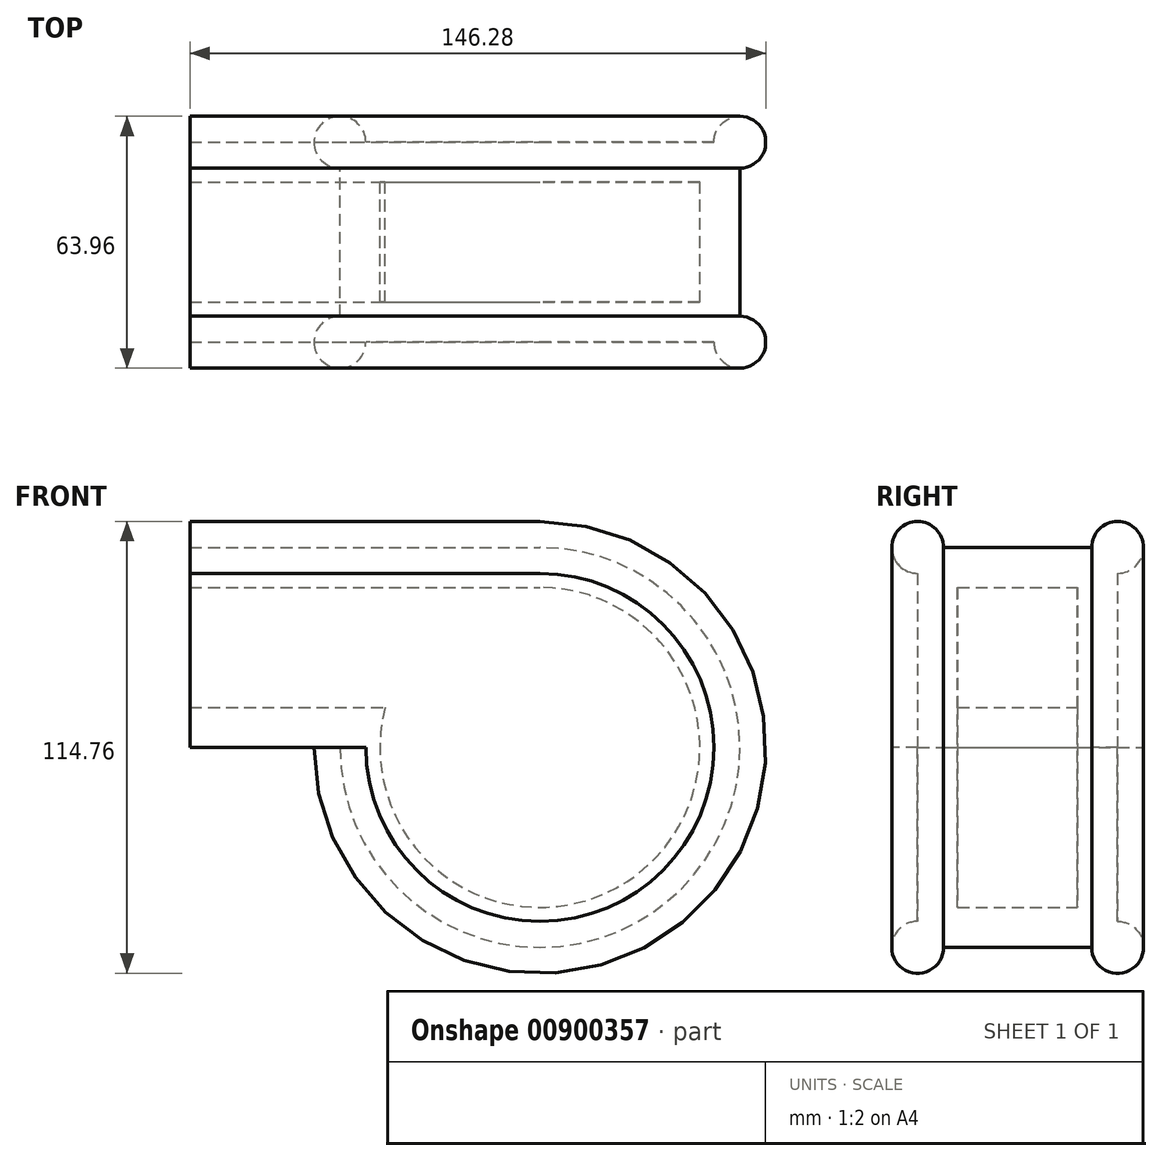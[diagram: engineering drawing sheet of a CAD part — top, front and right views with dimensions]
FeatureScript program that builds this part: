
annotation { "Feature Type Name" : "Feature", "Feature Type Description" : "" }
export const myFeature = defineFeature(function(context is Context, id is Id, definition is map)
    precondition{}
    {
        {
            var Q0;
            Q0=qCreatedBy(makeId("Front.planeOp"),FACE);
            var sketch = newSketch(context, id + "F0", { "sketchPlane" : qUnion([Q0])});
            skLineSegment(sketch, "E0.bottom", {"start": v(-50.8, 25.4) * mm, "end": v(38.1, 25.4) * mm});
            skLineSegment(sketch, "E0.top", {"start": v(-50.8, -25.4) * mm, "end": v(-12.7, -25.4) * mm});
            skLineSegment(sketch, "E0.left", {"start": v(-50.8, 25.4) * mm, "end": v(-50.8, -25.4) * mm});
            skArc(sketch, "E1", {"start": v(-12.7, -25.4) * mm, "mid": v(74.02, -61.32) * mm, "end": v(38.1, 25.4) * mm});
            skSolve(sketch);
        }
        {
            var Q0;
            Q0=makeQuery(id+"F0.imprint","IMPRINT",FACE,{"disambiguationData":[TD([[makeQuery(id+"F0.imprint","IMPRINT",EDGE,{"derivedFrom":sQuery(id+"F0.wireOp",EDGE,"E0.bottom")}),-1.0]])]});
            extrude(context, id + "F1", {"entities" : qUnion([Q0]), "depth" : 25.4 * mm, "offsetDistance" : 25.4 * mm, "hasSecondDirection" : true, "secondDirectionOppositeDirection" : true, "secondDirectionDepth" : 25.4 * mm});
        }
        {
            var Q0;
            Q0=makeQuery(id+"F1.opExtrude","SWEPT_FACE",FACE,{"disambiguationData":[OSD([sQuery(id+"F0.wireOp",EDGE,"E0.left")])]});
            shell(context, id + "F2", {"entities" : qUnion([Q0]), "thickness" : 10.16 * mm});
        }
        {
            var Q0;
            Q0=makeQuery(id+"F1.opExtrude","SWEPT_FACE",FACE,{"disambiguationData":[OSD([sQuery(id+"F0.wireOp",EDGE,"E0.left")])]});
            var sketch = newSketch(context, id + "F3", { "sketchPlane" : qUnion([Q0])});
            skSolve(sketch);
        }
        {
            var Q0;
            {var subQ0=sQuery(id+"F0.wireOp",EDGE,"E0.left");var subQ2=makeQuery(id+"F1.opExtrude","CAP_EDGE",EDGE,{"disambiguationData":[OSD([subQ0])],"isStart":true});Q0=makeQuery(id+"F3.imprint","IMPRINT",FACE,{"disambiguationData":[TD([[makeQuery(id+"F3.imprint","IMPRINT",EDGE,{"derivedFrom":subQ2}),1.0]])]});}
            var sketch = newSketch(context, id + "F4", { "sketchPlane" : qUnion([Q0])});
            skCircle(sketch, "E2", {"center": v(25.4, 25.4) * mm, "radius": 6.58 * mm});
            skSolve(sketch);
        }
        {
            var Q0;
            {var subQ0=sQuery(id+"F4.wireOp",EDGE,"E2");var subQ1=sQuery(id+"F0.wireOp",EDGE,"E0.left");var subQ4=makeQuery(id+"F3.imprint","IMPRINT",EDGE,{"derivedFrom":makeQuery(id+"F1.opExtrude","CAP_EDGE",EDGE,{"disambiguationData":[OSD([subQ1])],"isStart":false})});var subQ5=makeQuery(id+"F4.imprint","INTERSECT",VERTEX,{"derivedFrom":[subQ4,subQ0]});Q0=makeQuery(id+"F4.imprint","IMPRINT",FACE,{"disambiguationData":[TD([[makeQuery(id+"F4.imprint","IMPRINT",EDGE,{"disambiguationData":[TD([[subQ5,-1.0]])],"derivedFrom":subQ0}),1.0]])]});}
            var Q1;
            Q1=makeQuery(id+"F1.opExtrude","CAP_EDGE",EDGE,{"disambiguationData":[OSD([sQuery(id+"F0.wireOp",EDGE,"E0.bottom")])],"isStart":false});
            var Q2;
            Q2=makeQuery(id+"F1.opExtrude","CAP_EDGE",EDGE,{"disambiguationData":[OSD([sQuery(id+"F0.wireOp",EDGE,"E1")])],"isStart":false});
            sweep(context, id + "F5", {"operationType" : NewBodyOperationType.ADD, "profiles" : qUnion([Q0]), "path" : qUnion([Q1, Q2])});
        }
        {
            var Q0;
            Q0=makeQuery(id+"F1.opExtrude","SWEPT_BODY",BODY,{"disambiguationData":[OSD([sQuery(id+"F0.wireOp",EDGE,"E0.bottom"),sQuery(id+"F0.wireOp",EDGE,"E0.top"),sQuery(id+"F0.wireOp",EDGE,"E0.left"),sQuery(id+"F0.wireOp",EDGE,"E1")])]});
            var Q1;
            Q1=qCreatedBy(makeId("Front.planeOp"),FACE);
            mirror(context, id + "F6", {"operationType" : NewBodyOperationType.ADD, "entities" : qUnion([Q0]), "mirrorPlane" : qUnion([Q1])});
        }
    });
